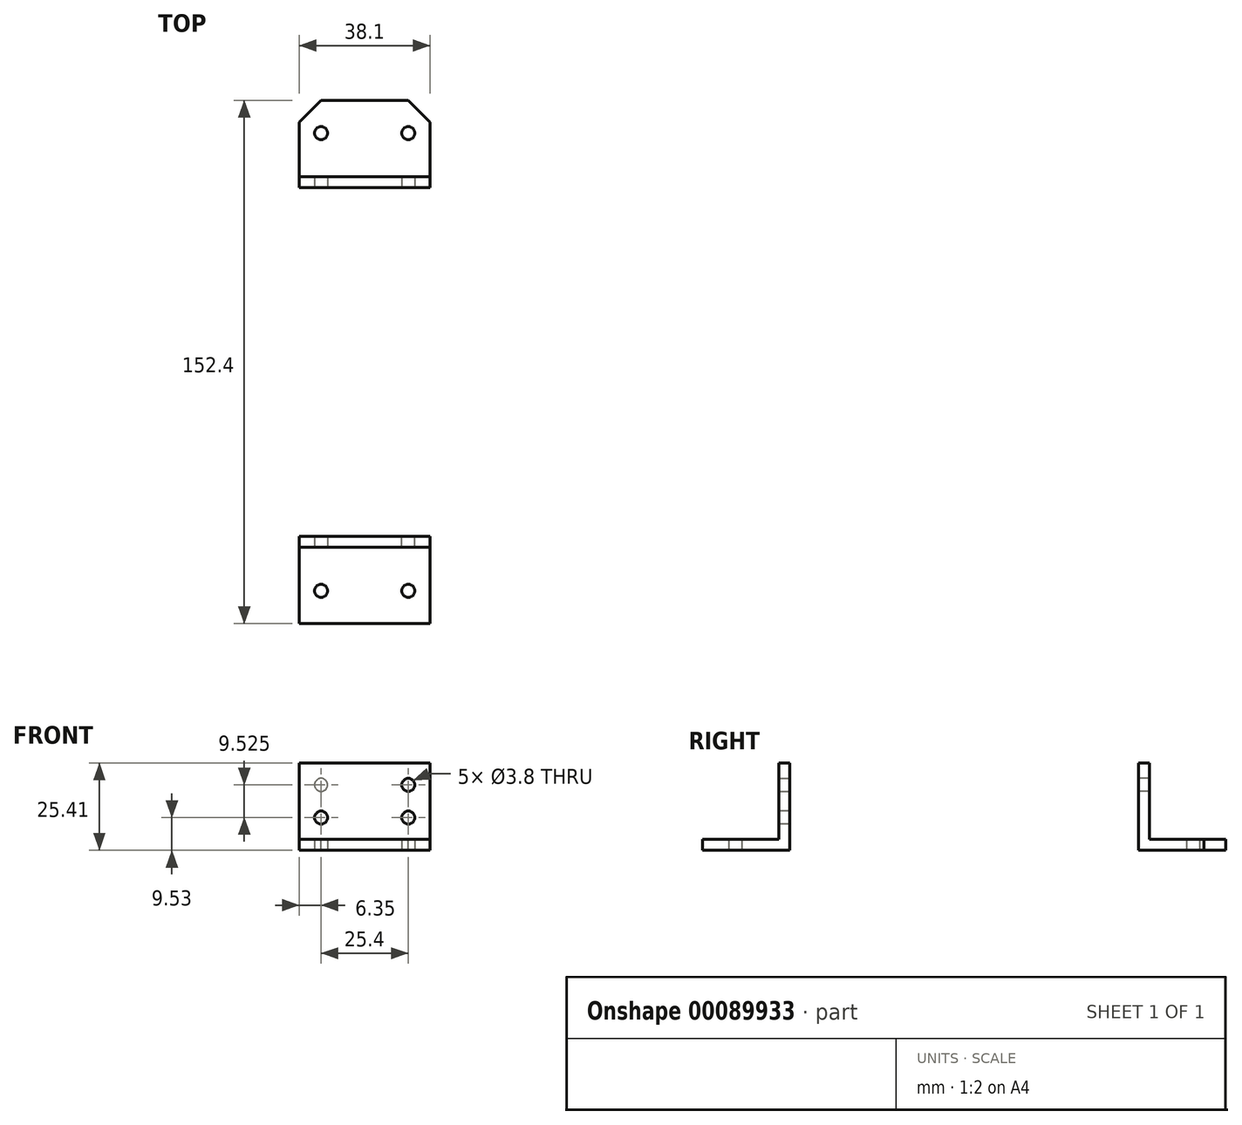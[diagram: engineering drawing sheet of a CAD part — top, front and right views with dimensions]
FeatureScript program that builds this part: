
annotation { "Feature Type Name" : "Feature", "Feature Type Description" : "" }
export const myFeature = defineFeature(function(context is Context, id is Id, definition is map)
    precondition{}
    {
        {
            var Q0;
            Q0=qCreatedBy(makeId("Front.planeOp"),FACE);
            var sketch = newSketch(context, id + "F0", { "sketchPlane" : qUnion([Q0])});
            skLineSegment(sketch, "E0.bottom", {"start": v(0, 0) * mm, "end": v(38.1, 0) * mm});
            skLineSegment(sketch, "E0.top", {"start": v(0, -3.18) * mm, "end": v(38.1, -3.18) * mm});
            skLineSegment(sketch, "E0.left", {"start": v(0, 0) * mm, "end": v(0, -3.18) * mm});
            skLineSegment(sketch, "E0.right", {"start": v(38.1, 0) * mm, "end": v(38.1, -3.18) * mm});
            skSolve(sketch);
        }
        {
            var Q0;
            Q0=makeQuery(id+"F0.imprint","IMPRINT",FACE,{"disambiguationData":[TD([[makeQuery(id+"F0.imprint","IMPRINT",EDGE,{"derivedFrom":sQuery(id+"F0.wireOp",EDGE,"E0.bottom")}),-1.0]])]});
            extrude(context, id + "F1", {"entities" : qUnion([Q0]), "depth" : 25.4 * mm});
        }
        {
            var Q0;
            Q0=makeQuery(id+"F1.opExtrude","SWEPT_FACE",FACE,{"disambiguationData":[OSD([sQuery(id+"F0.wireOp",EDGE,"E0.right")])]});
            var sketch = newSketch(context, id + "F2", { "sketchPlane" : qUnion([Q0])});
            skLineSegment(sketch, "E1.left", {"start": v(-25.4, -3.18) * mm, "end": v(-25.4, 22.23) * mm});
            skLineSegment(sketch, "E2", {"start": v(-25.4, -3.18) * mm, "end": v(-22.23, -3.18) * mm});
            skLineSegment(sketch, "E3", {"start": v(-22.23, -3.18) * mm, "end": v(-22.23, 22.22) * mm});
            skLineSegment(sketch, "E4", {"start": v(-22.23, 22.23) * mm, "end": v(-25.4, 22.23) * mm});
            skSolve(sketch);
        }
        {
            var Q0;
            {var subQ3=sQuery(id+"F2.wireOp",EDGE,"E4");Q0=makeQuery(id+"F2.imprint","IMPRINT",FACE,{"disambiguationData":[TD([[makeQuery(id+"F2.imprint","IMPRINT",EDGE,{"derivedFrom":subQ3}),1.0]])]});}
            extrude(context, id + "F3", {"entities" : qUnion([Q0]), "operationType" : NewBodyOperationType.ADD, "oppositeDirection" : true, "depth" : 38.1 * mm});
        }
        {
            var Q0;
            Q0=makeQuery(id+"F3.boolean.opBoolean","MERGE",FACE,{"derivedFrom":[makeQuery(id+"F1.opExtrude","CAP_FACE",FACE,{"disambiguationData":[OSD([sQuery(id+"F0.wireOp",EDGE,"E0.bottom"),sQuery(id+"F0.wireOp",EDGE,"E0.top"),sQuery(id+"F0.wireOp",EDGE,"E0.left"),sQuery(id+"F0.wireOp",EDGE,"E0.right")])],"isStart":false}),makeQuery(id+"F3.opExtrude","SWEPT_FACE",FACE,{"disambiguationData":[OSD([sQuery(id+"F2.wireOp",EDGE,"E1.left")])]})]});
            var sketch = newSketch(context, id + "F4", { "sketchPlane" : qUnion([Q0])});
            skPoint(sketch, "E5", {"position": v(6.35, 15.88) * mm});
            skPoint(sketch, "E6", {"position": v(31.75, 15.88) * mm});
            skSolve(sketch);
        }
        {
            var Q0;
            Q0=sQuery(id+"F4.wireOp",VERTEX,"E5");
            var Q1;
            Q1=sQuery(id+"F4.wireOp",VERTEX,"E6");
            var Q2;
            Q2=makeQuery(id+"F1.opExtrude","SWEPT_BODY",BODY,{"disambiguationData":[OSD([sQuery(id+"F0.wireOp",EDGE,"E0.bottom"),sQuery(id+"F0.wireOp",EDGE,"E0.top"),sQuery(id+"F0.wireOp",EDGE,"E0.left"),sQuery(id+"F0.wireOp",EDGE,"E0.right")])]});
            hole(context, id + "F5", {"style" : HoleStyle.SIMPLE, "endStyle" : HoleEndStyle.BLIND, "standardTappedOrClearance" : lookupTablePath({ "standard" : "ANSI", "fit" : "Normal (ASME)", "size" : "#6", "type" : "Clearance" }), "standardBlindInLast" : lookupTablePath({ "fit" : "Free", "standard" : "ANSI", "size" : "#6", "type" : "Clearance" }), "holeDiameter" : 3.8 * mm, "holeDepth" : 12.7 * mm, "locations" : qUnion([Q0, Q1]), "scope" : qUnion([Q2])});
        }
        {
            var Q0;
            Q0=makeQuery(id+"F1.opExtrude","SWEPT_FACE",FACE,{"disambiguationData":[OSD([sQuery(id+"F0.wireOp",EDGE,"E0.top")])]});
            var sketch = newSketch(context, id + "F6", { "sketchPlane" : qUnion([Q0])});
            skPoint(sketch, "E7", {"position": v(6.35, 9.53) * mm});
            skPoint(sketch, "E8", {"position": v(31.75, 9.53) * mm});
            skSolve(sketch);
        }
        {
            var Q0;
            Q0=sQuery(id+"F6.wireOp",VERTEX,"E7");
            var Q1;
            Q1=sQuery(id+"F6.wireOp",VERTEX,"E8");
            var Q2;
            Q2=makeQuery(id+"F1.opExtrude","SWEPT_BODY",BODY,{"disambiguationData":[OSD([sQuery(id+"F0.wireOp",EDGE,"E0.bottom"),sQuery(id+"F0.wireOp",EDGE,"E0.top"),sQuery(id+"F0.wireOp",EDGE,"E0.left"),sQuery(id+"F0.wireOp",EDGE,"E0.right")])]});
            hole(context, id + "F7", {"style" : HoleStyle.SIMPLE, "endStyle" : HoleEndStyle.BLIND, "standardTappedOrClearance" : lookupTablePath({ "standard" : "ANSI", "fit" : "Normal (ASME)", "size" : "#6", "type" : "Clearance" }), "standardBlindInLast" : lookupTablePath({ "fit" : "Free", "standard" : "ANSI", "size" : "#6", "type" : "Clearance" }), "holeDiameter" : 3.8 * mm, "holeDepth" : 12.7 * mm, "locations" : qUnion([Q0, Q1]), "scope" : qUnion([Q2])});
        }
        {
            var Q0;
            Q0=makeQuery(id+"F3.boolean.opBoolean","MERGE",FACE,{"derivedFrom":[makeQuery(id+"F1.opExtrude","CAP_FACE",FACE,{"disambiguationData":[OSD([sQuery(id+"F0.wireOp",EDGE,"E0.bottom"),sQuery(id+"F0.wireOp",EDGE,"E0.top"),sQuery(id+"F0.wireOp",EDGE,"E0.left"),sQuery(id+"F0.wireOp",EDGE,"E0.right")])],"isStart":false}),makeQuery(id+"F3.opExtrude","SWEPT_FACE",FACE,{"disambiguationData":[OSD([sQuery(id+"F2.wireOp",EDGE,"E1.left")])]})]});
            cPlane(context, id + "F8", {"entities" : qUnion([Q0]), "cplaneType" : CPlaneType.OFFSET, "offset" : 50.8 * mm, "width" : 152.4 * mm, "height" : 152.4 * mm});
        }
        {
            var Q0;
            Q0=makeQuery(id+"F1.opExtrude","SWEPT_BODY",BODY,{"disambiguationData":[OSD([sQuery(id+"F0.wireOp",EDGE,"E0.bottom"),sQuery(id+"F0.wireOp",EDGE,"E0.top"),sQuery(id+"F0.wireOp",EDGE,"E0.left"),sQuery(id+"F0.wireOp",EDGE,"E0.right")])]});
            var Q1;
            Q1=qCreatedBy(id+"F8.planeOp",FACE);
            mirror(context, id + "F9", {"entities" : qUnion([Q0]), "mirrorPlane" : qUnion([Q1])});
        }
        {
            var Q0;
            Q0=makeQuery(id+"F9.opPattern","COPY",FACE,{"derivedFrom":makeQuery(id+"F3.opExtrude","SWEPT_FACE",FACE,{"disambiguationData":[OSD([sQuery(id+"F2.wireOp",EDGE,"E3")])]}),"instanceName":"1"});
            var sketch = newSketch(context, id + "F10", { "sketchPlane" : qUnion([Q0])});
            skCircle(sketch, "E9", {"center": v(6.35, 15.88) * mm, "radius": 3.38 * mm});
            skSolve(sketch);
        }
        {
            var Q0;
            Q0=makeQuery(id+"F10.imprint","IMPRINT",FACE,{"disambiguationData":[TD([[makeQuery(id+"F10.imprint","IMPRINT",EDGE,{"derivedFrom":sQuery(id+"F10.wireOp",EDGE,"E9")}),1.0]])]});
            extrude(context, id + "F11", {"entities" : qUnion([Q0]), "oppositeDirection" : true, "depth" : 3.17 * mm});
        }
        {
            var Q0;
            Q0=makeQuery(id+"F11.opExtrude","SWEPT_BODY",BODY,{"disambiguationData":[OSD([sQuery(id+"F10.wireOp",EDGE,"E9")])]});
            var Q1;
            Q1=makeQuery(id+"F9.opPattern","COPY",BODY,{"derivedFrom":makeQuery(id+"F1.opExtrude","SWEPT_BODY",BODY,{"disambiguationData":[OSD([sQuery(id+"F0.wireOp",EDGE,"E0.bottom"),sQuery(id+"F0.wireOp",EDGE,"E0.top"),sQuery(id+"F0.wireOp",EDGE,"E0.left"),sQuery(id+"F0.wireOp",EDGE,"E0.right")])]}),"instanceName":"1"});
            booleanBodies(context, id + "F12", {"operationType" : BooleanOperationType.UNION, "tools" : qUnion([Q0, Q1])});
        }
        {
            var Q0;
            Q0=makeQuery(id+"F12.opBoolean","MERGE",FACE,{"derivedFrom":[makeQuery(id+"F9.opPattern","COPY",FACE,{"derivedFrom":makeQuery(id+"F3.opExtrude","SWEPT_FACE",FACE,{"disambiguationData":[OSD([sQuery(id+"F2.wireOp",EDGE,"E3")])]}),"instanceName":"1"}),makeQuery(id+"F11.opExtrude","CAP_FACE",FACE,{"disambiguationData":[OSD([sQuery(id+"F10.wireOp",EDGE,"E9")])],"isStart":true})]});
            var sketch = newSketch(context, id + "F13", { "sketchPlane" : qUnion([Q0])});
            skPoint(sketch, "E10", {"position": v(19.05, 6.35) * mm});
            skPoint(sketch, "E10.positionSnap0", {"position": v(19.05, 22.23) * mm});
            skPoint(sketch, "E11", {"position": v(6.35, 6.35) * mm});
            skPoint(sketch, "E12", {"position": v(31.75, 6.35) * mm});
            skSolve(sketch);
        }
        {
            var Q0;
            Q0=sQuery(id+"F13.wireOp",VERTEX,"E12");
            var Q1;
            Q1=sQuery(id+"F13.wireOp",VERTEX,"E11");
            var Q2;
            Q2=makeQuery(id+"F11.opExtrude","SWEPT_BODY",BODY,{"disambiguationData":[OSD([sQuery(id+"F10.wireOp",EDGE,"E9")])]});
            hole(context, id + "F14", {"style" : HoleStyle.SIMPLE, "endStyle" : HoleEndStyle.BLIND, "standardTappedOrClearance" : lookupTablePath({ "standard" : "ANSI", "fit" : "Normal (ASME)", "size" : "#6", "type" : "Clearance" }), "standardBlindInLast" : lookupTablePath({ "fit" : "Free", "standard" : "ANSI", "size" : "#6", "type" : "Clearance" }), "holeDiameter" : 3.8 * mm, "holeDepth" : 12.7 * mm, "locations" : qUnion([Q0, Q1]), "scope" : qUnion([Q2])});
        }
        {
            var Q0;
            {var subQ0=sQuery(id+"F2.wireOp",EDGE,"E3");Q0=makeQuery(id+"F12.opBoolean","MERGE",FACE,{"derivedFrom":[makeQuery(id+"F9.opPattern","COPY",FACE,{"derivedFrom":makeQuery(id+"F3.opExtrude","SWEPT_FACE",FACE,{"disambiguationData":[OSD([subQ0])]}),"instanceName":"1"}),makeQuery(id+"F11.opExtrude","CAP_FACE",FACE,{"disambiguationData":[OSD([subQ0,sQuery(id+"F5.hole-0.sketch.wireOp",EDGE,"core_line_2"),sQuery(id+"F10.wireOp",EDGE,"E9")])],"isStart":true})]});}
            var sketch = newSketch(context, id + "F15", { "sketchPlane" : qUnion([Q0])});
            skPoint(sketch, "E13.oppositeSnap0", {"position": v(38.1, 11.11) * mm});
            skLineSegment(sketch, "E13.bottom", {"start": v(2.77, 18.81) * mm, "end": v(34.65, 18.81) * mm});
            skLineSegment(sketch, "E13.top", {"start": v(2.77, 11.11) * mm, "end": v(34.65, 11.11) * mm});
            skLineSegment(sketch, "E13.left", {"start": v(2.77, 18.81) * mm, "end": v(2.77, 11.11) * mm});
            skLineSegment(sketch, "E13.right", {"start": v(34.65, 18.81) * mm, "end": v(34.65, 11.11) * mm});
            skSolve(sketch);
        }
        {
            var Q0;
            Q0=makeQuery(id+"F15.imprint","IMPRINT",FACE,{"disambiguationData":[TD([[makeQuery(id+"F15.imprint","IMPRINT",EDGE,{"derivedFrom":makeQuery(id+"F9.opPattern","COPY",EDGE,{"derivedFrom":makeQuery(id+"F5.hole-1.boolean.opBoolean","INTERSECT",EDGE,{"derivedFrom":[makeQuery(id+"F3.opExtrude","SWEPT_FACE",FACE,{"disambiguationData":[OSD([sQuery(id+"F2.wireOp",EDGE,"E3")])]}),makeQuery(id+"F5.hole-1.opRevolve","SWEPT_FACE",FACE,{"disambiguationData":[OSD([sQuery(id+"F5.hole-1.sketch.wireOp",EDGE,"core_line_2")])]})]}),"instanceName":"1"})}),1.0]])]});
            var Q1;
            Q1=makeQuery(id+"F15.imprint","IMPRINT",FACE,{"disambiguationData":[TD([[makeQuery(id+"F15.imprint","IMPRINT",EDGE,{"derivedFrom":makeQuery(id+"F11.opExtrude","CAP_EDGE",EDGE,{"disambiguationData":[OSD([sQuery(id+"F2.wireOp",EDGE,"E3"),sQuery(id+"F5.hole-0.sketch.wireOp",EDGE,"core_line_2")])],"isStart":true})}),1.0]])]});
            extrude(context, id + "F16", {"entities" : qUnion([Q0, Q1]), "operationType" : NewBodyOperationType.ADD, "oppositeDirection" : true, "depth" : 3.17 * mm});
        }
        {
            var Q0;
            Q0=makeQuery(id+"F1.opExtrude","SWEPT_FACE",FACE,{"disambiguationData":[OSD([sQuery(id+"F0.wireOp",EDGE,"E0.bottom")])]});
            var sketch = newSketch(context, id + "F17", { "sketchPlane" : qUnion([Q0])});
            skLineSegment(sketch, "E14", {"start": v(0, 0) * mm, "end": v(6.35, 0) * mm});
            skLineSegment(sketch, "E15", {"start": v(0, 0) * mm, "end": v(0, -6.35) * mm});
            skLineSegment(sketch, "E16", {"start": v(0, -6.35) * mm, "end": v(6.35, 0) * mm});
            skLineSegment(sketch, "E17", {"start": v(19.05, 0) * mm, "end": v(19.05, -5.44) * mm});
            skLineSegment(sketch, "E18.MirrorCS", {"start": v(38.1, -6.35) * mm, "end": v(31.75, 0) * mm});
            skLineSegment(sketch, "E19.MirrorCS", {"start": v(38.1, 0) * mm, "end": v(31.75, 0) * mm});
            skLineSegment(sketch, "E20.MirrorCS", {"start": v(38.1, 0) * mm, "end": v(38.1, -6.35) * mm});
            skSolve(sketch);
        }
        {
            var Q0;
            Q0=makeQuery(id+"F17.imprint","IMPRINT",FACE,{"disambiguationData":[TD([[makeQuery(id+"F17.imprint","IMPRINT",EDGE,{"derivedFrom":sQuery(id+"F17.wireOp",EDGE,"E14")}),-1.0]])]});
            var Q1;
            Q1=makeQuery(id+"F17.imprint","IMPRINT",FACE,{"disambiguationData":[TD([[makeQuery(id+"F17.imprint","IMPRINT",EDGE,{"derivedFrom":sQuery(id+"F17.wireOp",EDGE,"E18.MirrorCS")}),-1.0]])]});
            extrude(context, id + "F18", {"entities" : qUnion([Q0, Q1]), "operationType" : NewBodyOperationType.REMOVE, "oppositeDirection" : true, "depth" : 25.4 * mm});
        }
    });
